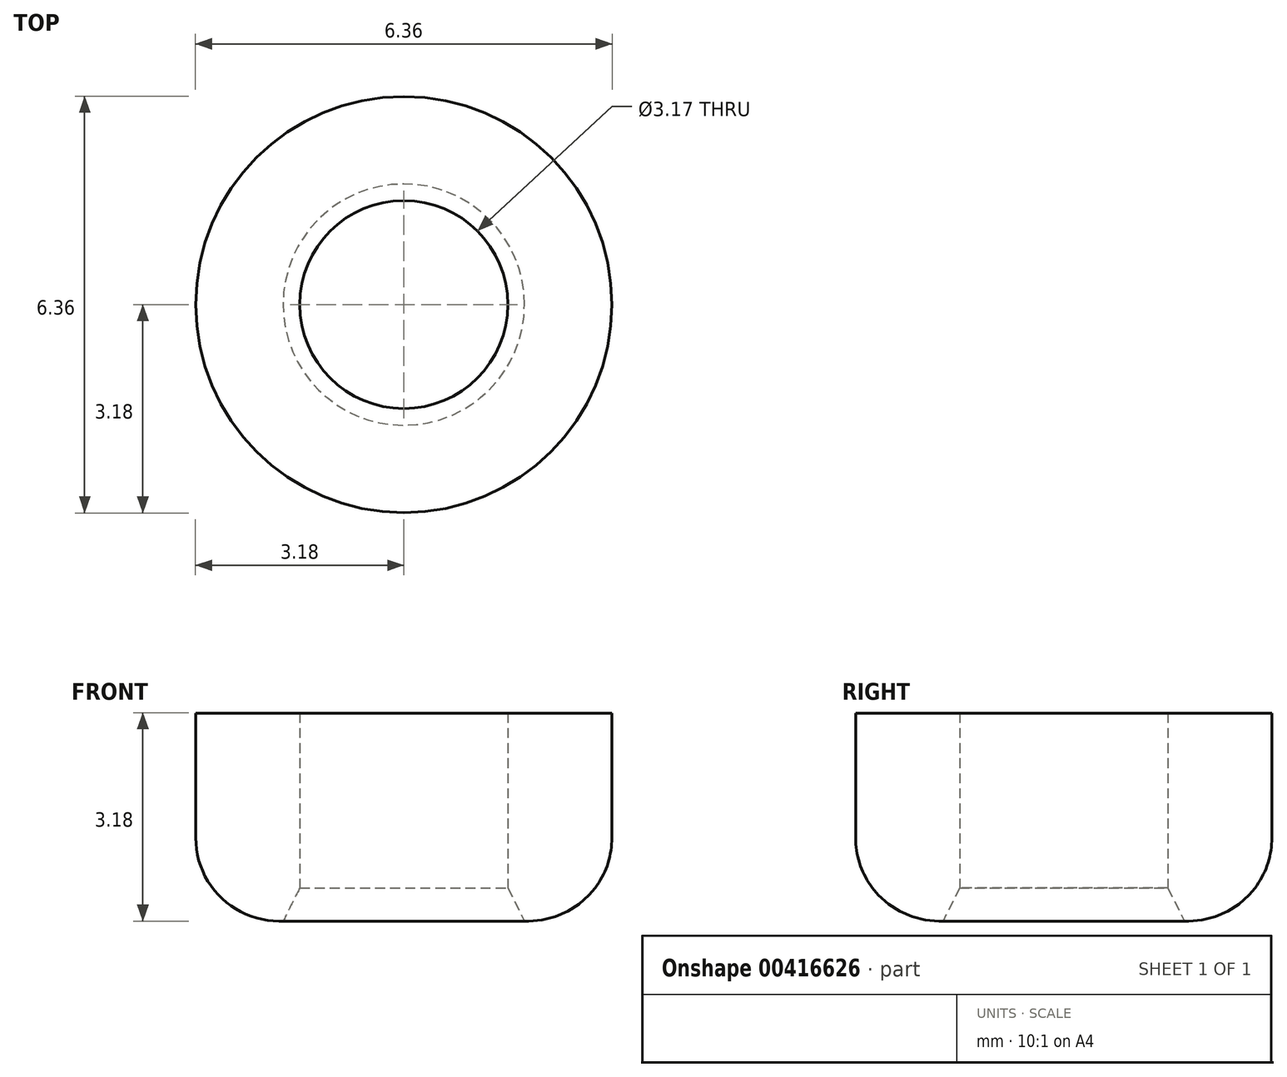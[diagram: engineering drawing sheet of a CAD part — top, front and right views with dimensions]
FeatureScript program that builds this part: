
annotation { "Feature Type Name" : "Feature", "Feature Type Description" : "" }
export const myFeature = defineFeature(function(context is Context, id is Id, definition is map)
    precondition{}
    {
        {
            var Q0;
            Q0=qCreatedBy(makeId("Front.planeOp"),FACE);
            var sketch = newSketch(context, id + "F0", { "sketchPlane" : qUnion([Q0])});
            skLineSegment(sketch, "E0", {"start": v(-1.59, 0) * mm, "end": v(-3.18, 0) * mm});
            skLineSegment(sketch, "E1", {"start": v(-3.18, 0) * mm, "end": v(-3.18, 3.17) * mm});
            skLineSegment(sketch, "E2", {"start": v(-3.18, 3.18) * mm, "end": v(-1.59, 3.18) * mm});
            skLineSegment(sketch, "E3.0", {"start": v(-1.59, 3.18) * mm, "end": v(-1.59, 0) * mm});
            skLineSegment(sketch, "E4", {"start": v(0, 0) * mm, "end": v(0, 6.65) * mm, "construction": true});
            skSolve(sketch);
        }
        {
            var Q0;
            Q0=makeQuery(id+"F0.imprint","IMPRINT",FACE,{"disambiguationData":[TD([[makeQuery(id+"F0.imprint","IMPRINT",EDGE,{"derivedFrom":sQuery(id+"F0.wireOp",EDGE,"E0")}),-1.0]])]});
            var Q1;
            Q1=sQuery(id+"F0.wireOp",EDGE,"E4");
            revolve(context, id + "F1", {"entities" : qUnion([Q0]), "axis" : qUnion([Q1]), "revolveType" : RevolveType.FULL});
        }
        {
            var Q0;
            Q0=makeQuery(id+"F1.opRevolve","SWEPT_EDGE",EDGE,{"disambiguationData":[OSD([sQuery(id+"F0.wireOp",EDGE,"E0"),sQuery(id+"F0.wireOp",EDGE,"E1")])]});
            fillet(context, id + "F2", {"entities" : qUnion([Q0]), "radius" : 1.27 * mm, "tangentPropagation" : true, "allowEdgeOverflow" : false});
        }
        {
            var Q0;
            Q0=makeQuery(id+"F1.opRevolve","SWEPT_EDGE",EDGE,{"disambiguationData":[OSD([sQuery(id+"F0.wireOp",EDGE,"E0"),sQuery(id+"F0.wireOp",EDGE,"E3.0")])]});
            chamfer(context, id + "F3", {"entities" : qUnion([Q0]), "chamferType" : ChamferType.TWO_OFFSETS, "width1" : 0.5 * mm, "oppositeDirection" : false, "width2" : 0.25 * mm, "tangentPropagation" : true});
        }
    });
